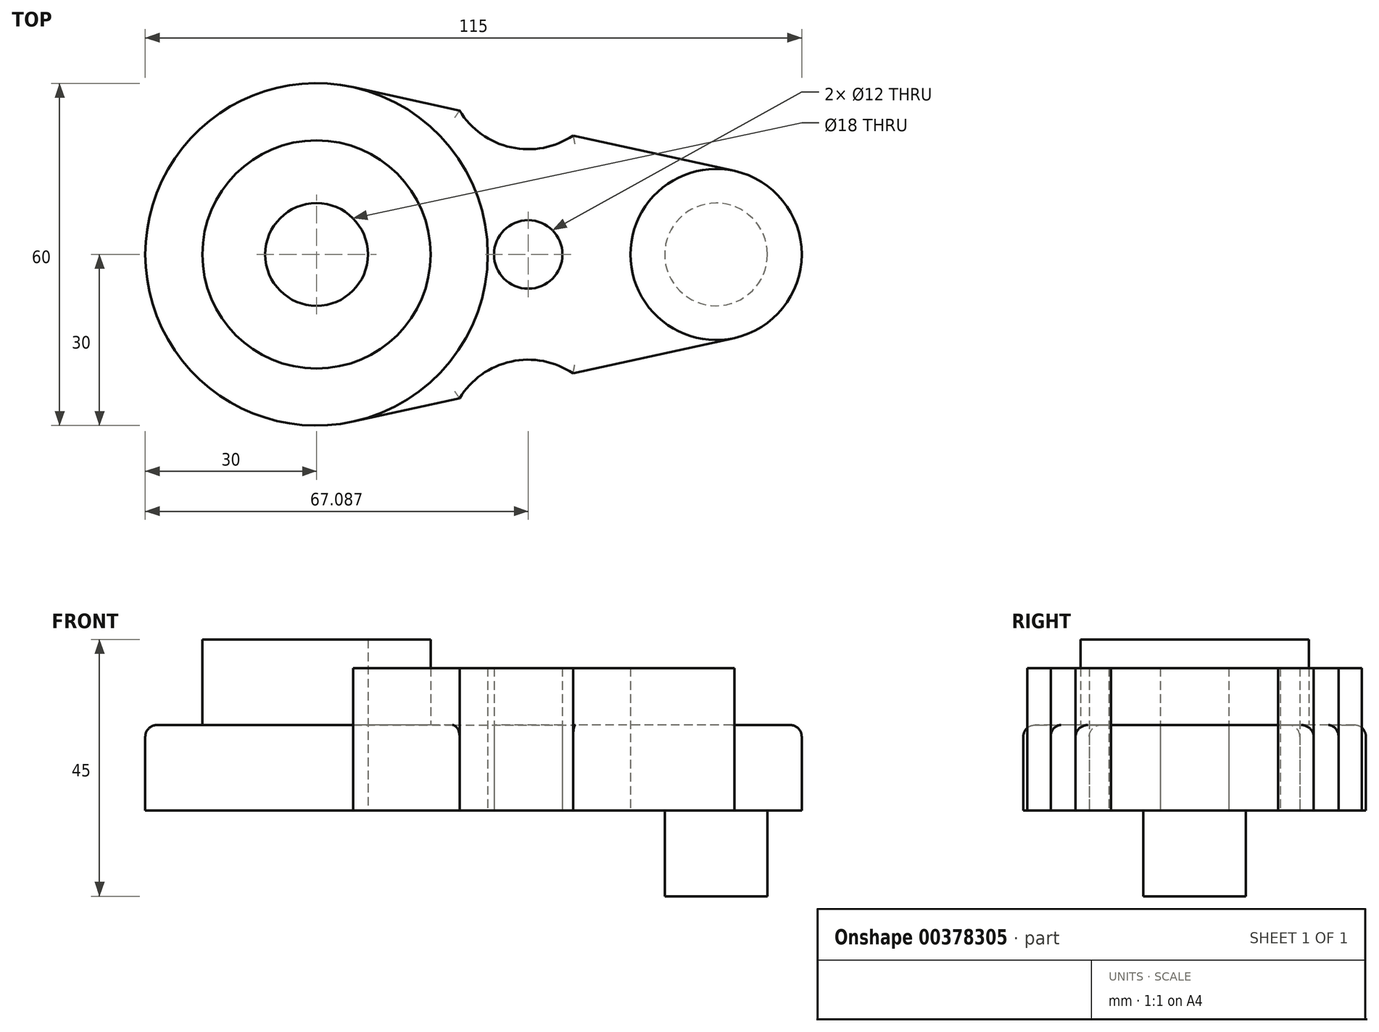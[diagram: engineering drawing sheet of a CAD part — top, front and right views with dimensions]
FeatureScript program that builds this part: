
annotation { "Feature Type Name" : "Feature", "Feature Type Description" : "" }
export const myFeature = defineFeature(function(context is Context, id is Id, definition is map)
    precondition{}
    {
        {
            var Q0;
            Q0=qCreatedBy(makeId("Top.planeOp"),FACE);
            var sketch = newSketch(context, id + "F0", { "sketchPlane" : qUnion([Q0])});
            skCircle(sketch, "E0", {"center": v(-53.43, 0) * mm, "radius": 30 * mm});
            skCircle(sketch, "E1", {"center": v(16.57, 0) * mm, "radius": 15 * mm});
            skLineSegment(sketch, "E2", {"start": v(19.78, 14.65) * mm, "end": v(-47, 29.3) * mm});
            skLineSegment(sketch, "E3", {"start": v(-47, -29.3) * mm, "end": v(19.78, -14.65) * mm});
            skCircle(sketch, "E4", {"center": v(-53.43, 0) * mm, "radius": 20 * mm});
            skCircle(sketch, "E5", {"center": v(16.57, 0) * mm, "radius": 9 * mm});
            skCircle(sketch, "E6", {"center": v(-53.43, 0) * mm, "radius": 9 * mm});
            skLineSegment(sketch, "E7", {"start": v(-16.34, 37.9) * mm, "end": v(-16.34, -37.9) * mm});
            skCircle(sketch, "E8", {"center": v(-16.34, 32.5) * mm, "radius": 14.06 * mm});
            skCircle(sketch, "E9.MirrorC", {"center": v(-16.34, -32.5) * mm, "radius": 14.06 * mm});
            skCircle(sketch, "E10", {"center": v(-16.34, 0) * mm, "radius": 6 * mm});
            skSolve(sketch);
        }
        {
            var Q0;
            Q0=makeQuery(id+"F0.imprint","IMPRINT",FACE,{"disambiguationData":[TD([[makeQuery(id+"F0.imprint","IMPRINT",EDGE,{"derivedFrom":sQuery(id+"F0.wireOp",EDGE,"E4")}),-1.0]])]});
            var Q1;
            Q1=makeQuery(id+"F0.imprint","IMPRINT",FACE,{"disambiguationData":[TD([[makeQuery(id+"F0.imprint","IMPRINT",EDGE,{"derivedFrom":sQuery(id+"F0.wireOp",EDGE,"E4")}),1.0]])]});
            var Q2;
            {var subQ1=sQuery(id+"F0.wireOp",EDGE,"E0");var subQ5=sQuery(id+"F0.wireOp",EDGE,"E2");var subQ6=makeQuery(id+"F0.imprint","INTERSECT",VERTEX,{"derivedFrom":[subQ1,subQ5]});Q2=makeQuery(id+"F0.imprint","IMPRINT",FACE,{"disambiguationData":[TD([[makeQuery(id+"F0.imprint","IMPRINT",EDGE,{"disambiguationData":[TD([[subQ6,1.0]])],"derivedFrom":subQ1}),-1.0]])]});}
            var Q3;
            {var subQ6=sQuery(id+"F0.wireOp",EDGE,"E1");var subQ9=sQuery(id+"F0.wireOp",EDGE,"E2");var subQ10=makeQuery(id+"F0.imprint","INTERSECT",VERTEX,{"derivedFrom":[subQ6,subQ9]});Q3=makeQuery(id+"F0.imprint","IMPRINT",FACE,{"disambiguationData":[TD([[makeQuery(id+"F0.imprint","IMPRINT",EDGE,{"disambiguationData":[TD([[subQ10,-1.0]])],"derivedFrom":subQ6}),-1.0]])]});}
            var Q4;
            Q4=makeQuery(id+"F0.imprint","IMPRINT",FACE,{"disambiguationData":[TD([[makeQuery(id+"F0.imprint","IMPRINT",EDGE,{"derivedFrom":sQuery(id+"F0.wireOp",EDGE,"E5")}),-1.0]])]});
            var Q5;
            Q5=makeQuery(id+"F0.imprint","IMPRINT",FACE,{"disambiguationData":[TD([[makeQuery(id+"F0.imprint","IMPRINT",EDGE,{"derivedFrom":sQuery(id+"F0.wireOp",EDGE,"E5")}),1.0]])]});
            extrude(context, id + "F1", {"entities" : qUnion([Q0, Q1, Q2, Q3, Q4, Q5]), "depth" : 15 * mm});
        }
        {
            var Q0;
            Q0=makeQuery(id+"F0.imprint","IMPRINT",FACE,{"disambiguationData":[TD([[makeQuery(id+"F0.imprint","IMPRINT",EDGE,{"derivedFrom":sQuery(id+"F0.wireOp",EDGE,"E5")}),1.0]])]});
            extrude(context, id + "F2", {"entities" : qUnion([Q0]), "operationType" : NewBodyOperationType.ADD, "oppositeDirection" : true, "depth" : 15 * mm});
        }
        {
            var Q0;
            Q0=makeQuery(id+"F0.imprint","IMPRINT",FACE,{"disambiguationData":[TD([[makeQuery(id+"F0.imprint","IMPRINT",EDGE,{"derivedFrom":sQuery(id+"F0.wireOp",EDGE,"E4")}),1.0]])]});
            var Q1;
            Q1=sQuery(id+"F0.wireOp",EDGE,"E4");
            extrude(context, id + "F3", {"entities" : qUnion([Q0]), "operationType" : NewBodyOperationType.ADD, "surfaceEntities" : qUnion([Q1]), "depth" : 30 * mm});
        }
        {
            var Q0;
            Q0=makeQuery(id+"F1.opExtrude","CAP_EDGE",EDGE,{"disambiguationData":[OSD([sQuery(id+"F0.wireOp",EDGE,"E0")])],"isStart":false});
            var Q1;
            Q1=makeQuery(id+"F1.opExtrude","CAP_EDGE",EDGE,{"disambiguationData":[OSD([sQuery(id+"F0.wireOp",EDGE,"E9.MirrorC")])],"isStart":false});
            var Q2;
            Q2=makeQuery(id+"F1.opExtrude","CAP_EDGE",EDGE,{"disambiguationData":[OSD([sQuery(id+"F0.wireOp",EDGE,"E8")])],"isStart":false});
            var Q3;
            {var subQ0=sQuery(id+"F0.wireOp",EDGE,"E3");Q3=makeQuery(id+"F1.opExtrude","CAP_EDGE",EDGE,{"disambiguationData":[OSD([subQ0]),TDD([makeQuery(id+"F0.imprint","IMPRINT",EDGE,{"disambiguationData":[TD([[makeQuery(id+"F0.imprint","INTERSECT",VERTEX,{"derivedFrom":[sQuery(id+"F0.wireOp",EDGE,"E1"),subQ0]}),1.0]])],"derivedFrom":subQ0})])],"isStart":false});}
            fillet(context, id + "F4", {"entities" : qUnion([Q0, Q1, Q2, Q3]), "radius" : 2 * mm, "tangentPropagation" : true, "allowEdgeOverflow" : false});
        }
        {
            var Q0;
            {var subQ0=sQuery(id+"F0.wireOp",EDGE,"E10");var subQ1=sQuery(id+"F0.wireOp",EDGE,"E7");var subQ2=makeQuery(id+"F0.imprint","INTERSECT",VERTEX,{"disambiguationData":[OD(0.0)],"derivedFrom":[subQ1,subQ0]});Q0=makeQuery(id+"F0.imprint","IMPRINT",FACE,{"disambiguationData":[TD([[makeQuery(id+"F0.imprint","IMPRINT",EDGE,{"disambiguationData":[TD([[subQ2,-1.0]])],"derivedFrom":subQ1}),-1.0]])]});}
            var Q1;
            {var subQ0=sQuery(id+"F0.wireOp",EDGE,"E10");var subQ1=sQuery(id+"F0.wireOp",EDGE,"E7");var subQ2=makeQuery(id+"F0.imprint","INTERSECT",VERTEX,{"disambiguationData":[OD(0.0)],"derivedFrom":[subQ1,subQ0]});Q1=makeQuery(id+"F0.imprint","IMPRINT",FACE,{"disambiguationData":[TD([[makeQuery(id+"F0.imprint","IMPRINT",EDGE,{"disambiguationData":[TD([[subQ2,-1.0]])],"derivedFrom":subQ1}),1.0]])]});}
            extrude(context, id + "F5", {"entities" : qUnion([Q0, Q1]), "depth" : 25 * mm});
        }
    });
